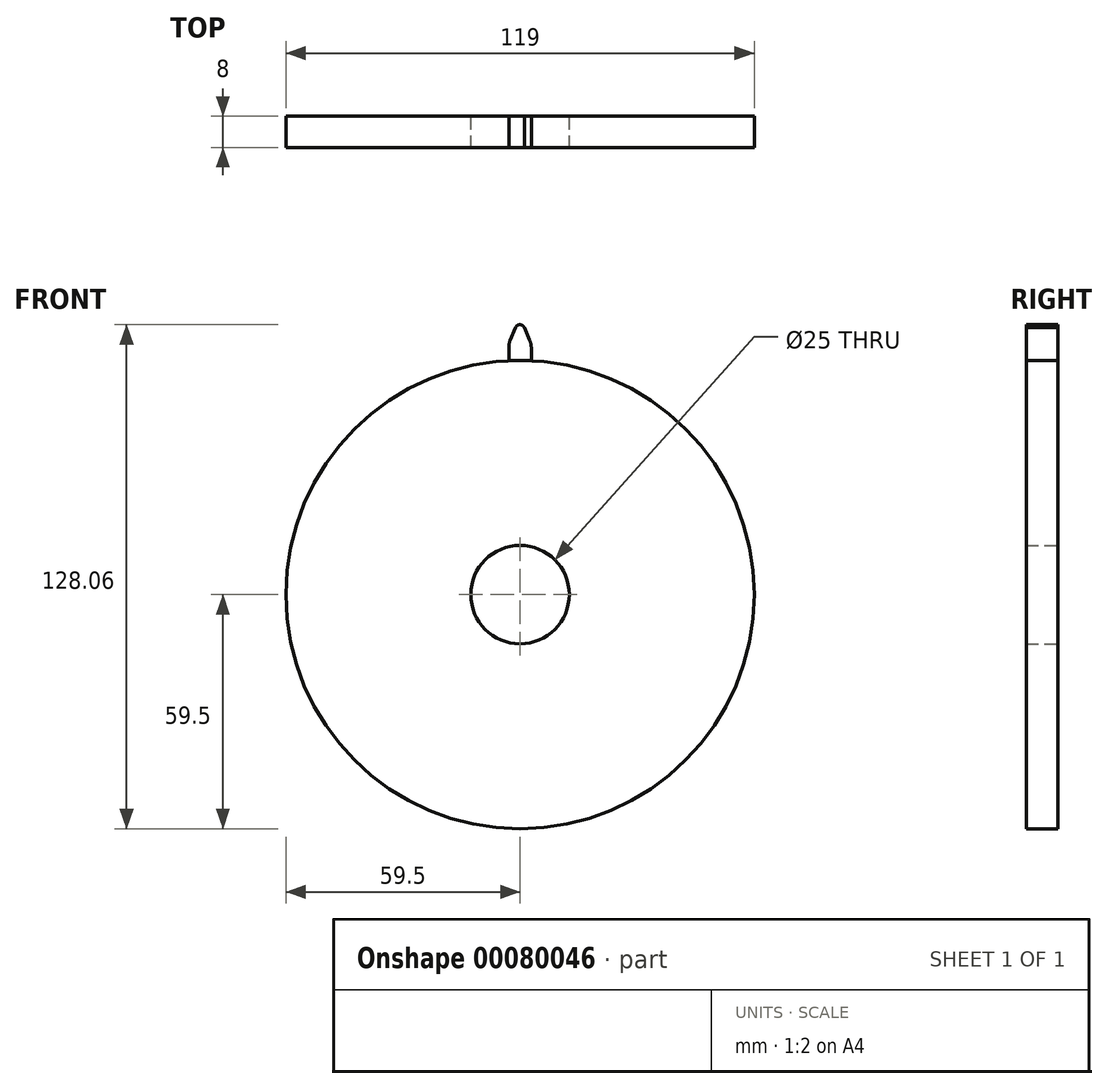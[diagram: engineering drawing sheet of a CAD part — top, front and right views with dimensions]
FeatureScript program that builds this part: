
annotation { "Feature Type Name" : "Feature", "Feature Type Description" : "" }
export const myFeature = defineFeature(function(context is Context, id is Id, definition is map)
    precondition{}
    {
        {
            var Q0;
            Q0=qCreatedBy(makeId("Front.planeOp"),FACE);
            var sketch = newSketch(context, id + "F0", { "sketchPlane" : qUnion([Q0])});
            skCircle(sketch, "E0", {"center": v(0, 0) * mm, "radius": 12.5 * mm});
            skCircle(sketch, "E1", {"center": v(0, 0) * mm, "radius": 59.5 * mm});
            skLineSegment(sketch, "E2", {"start": v(-2.86, 63.69) * mm, "end": v(-2.86, 59.43) * mm});
            skLineSegment(sketch, "E3.MirrorCS", {"start": v(2.86, 63.69) * mm, "end": v(2.86, 59.43) * mm});
            skArc(sketch, "E4", {"start": v(2.86, 59.43) * mm, "mid": v(0, 59.5) * mm, "end": v(-2.86, 59.43) * mm});
            skPoint(sketch, "E5.MirrorCS.end.orphan", {"position": v(2.87, 63.69) * mm});
            skPoint(sketch, "E5.MirrorCS.start.orphan", {"position": v(0, 67.8) * mm});
            skLineSegment(sketch, "E6", {"start": v(-2.86, 63.69) * mm, "end": v(-1.2, 67.79) * mm});
            skLineSegment(sketch, "E7", {"start": v(2.86, 63.69) * mm, "end": v(1.1, 67.8) * mm});
            skArc(sketch, "E8", {"start": v(1.1, 67.8) * mm, "mid": v(-0.05, 68.56) * mm, "end": v(-1.2, 67.79) * mm});
            skPoint(sketch, "E9.start.orphan", {"position": v(0, 59.5) * mm});
            skSolve(sketch);
        }
        {
            var Q0;
            Q0=makeQuery(id+"F0.imprint","IMPRINT",FACE,{"disambiguationData":[TD([[makeQuery(id+"F0.imprint","IMPRINT",EDGE,{"derivedFrom":sQuery(id+"F0.wireOp",EDGE,"E0")}),-1.0]])]});
            extrude(context, id + "F1", {"entities" : qUnion([Q0]), "depth" : 8 * mm});
        }
        {
            var Q0;
            {var subQ1=sQuery(id+"F0.wireOp",EDGE,"E2");Q0=makeQuery(id+"F0.imprint","IMPRINT",FACE,{"disambiguationData":[TD([[makeQuery(id+"F0.imprint","IMPRINT",EDGE,{"derivedFrom":subQ1}),1.0]])]});}
            var Q1;
            Q1=makeQuery(id+"F1.opExtrude","CAP_FACE",FACE,{"disambiguationData":[OSD([sQuery(id+"F0.wireOp",EDGE,"E0"),sQuery(id+"F0.wireOp",EDGE,"E1")])],"isStart":false});
            extrude(context, id + "F2", {"entities" : qUnion([Q0]), "endBound" : BoundingType.UP_TO_SURFACE, "endBoundEntityFace" : qUnion([Q1]), "depth" : 25 * mm});
        }
        {
            var Q0;
            Q0=makeQuery(id+"F2.opExtrude","SWEPT_EDGE",EDGE,{"disambiguationData":[OSD([sQuery(id+"F0.wireOp",EDGE,"E3.MirrorCS"),sQuery(id+"F0.wireOp",EDGE,"E7")])]});
            var Q1;
            Q1=makeQuery(id+"F2.opExtrude","SWEPT_EDGE",EDGE,{"disambiguationData":[OSD([sQuery(id+"F0.wireOp",EDGE,"E2"),sQuery(id+"F0.wireOp",EDGE,"E6")])]});
            fillet(context, id + "F3", {"entities" : qUnion([Q0, Q1]), "radius" : 5 * mm, "tangentPropagation" : true, "allowEdgeOverflow" : false});
        }
    });
